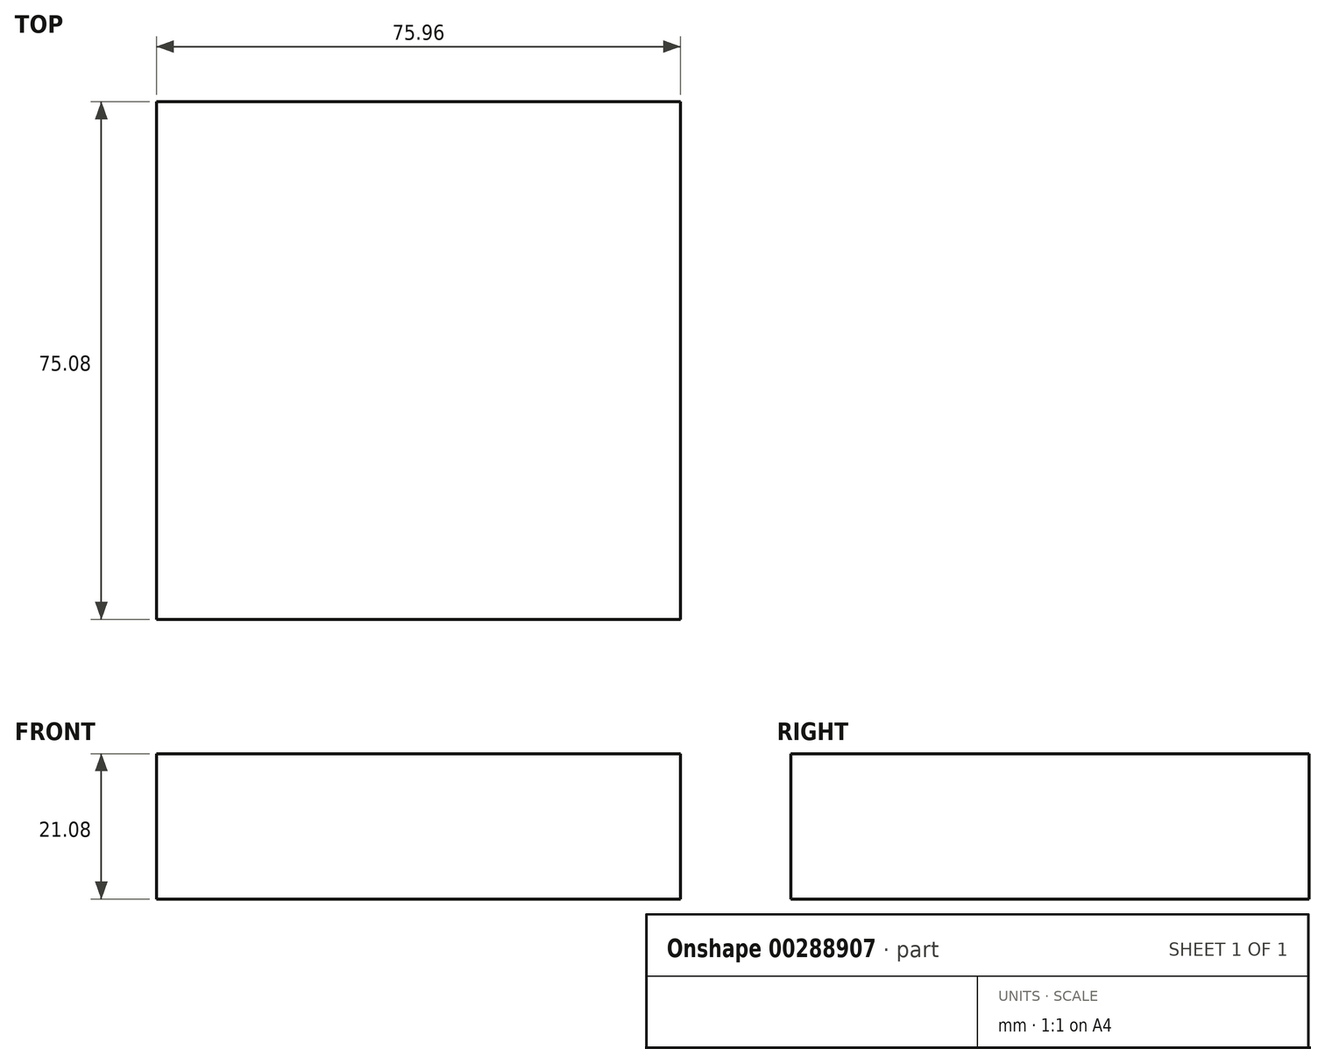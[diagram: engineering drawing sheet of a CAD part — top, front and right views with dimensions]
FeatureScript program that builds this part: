
annotation { "Feature Type Name" : "Feature", "Feature Type Description" : "" }
export const myFeature = defineFeature(function(context is Context, id is Id, definition is map)
    precondition{}
    {
        {
            var Q0;
            Q0=qCreatedBy(makeId("Top.planeOp"),FACE);
            var sketch = newSketch(context, id + "F0", { "sketchPlane" : qUnion([Q0])});
            skLineSegment(sketch, "E0.bottom", {"start": v(0, 0) * mm, "end": v(75.96, 0) * mm});
            skLineSegment(sketch, "E0.top", {"start": v(0, 75.08) * mm, "end": v(75.96, 75.08) * mm});
            skLineSegment(sketch, "E0.left", {"start": v(0, 0) * mm, "end": v(0, 75.08) * mm});
            skLineSegment(sketch, "E0.right", {"start": v(75.96, 0) * mm, "end": v(75.96, 75.08) * mm});
            skSolve(sketch);
        }
        {
            var Q0;
            Q0 = qSketchRegion(id + "F0", true);
            extrude(context, id + "F1", {"entities" : qUnion([Q0]), "oppositeDirection" : true, "depth" : 2.54 * mm});
        }
        {
            var Q0;
            Q0=makeQuery(id+"F1.opExtrude","CAP_FACE",FACE,{"disambiguationData":[OSD([sQuery(id+"F0.wireOp",EDGE,"E0.bottom"),sQuery(id+"F0.wireOp",EDGE,"E0.top"),sQuery(id+"F0.wireOp",EDGE,"E0.left"),sQuery(id+"F0.wireOp",EDGE,"E0.right")])],"isStart":true});
            extrude(context, id + "F2", {"entities" : qUnion([Q0]), "operationType" : NewBodyOperationType.ADD, "depth" : 18.54 * mm});
        }
    });
